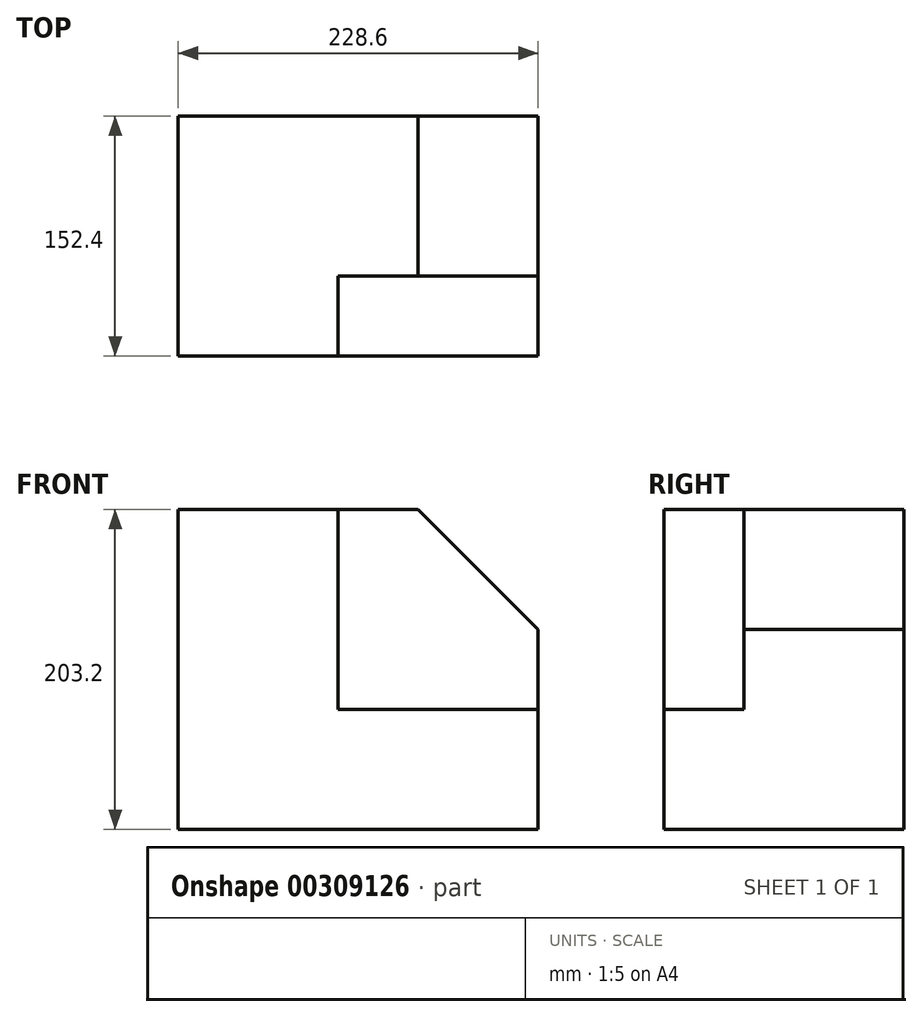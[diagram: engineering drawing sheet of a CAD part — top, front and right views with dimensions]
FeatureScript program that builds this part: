
annotation { "Feature Type Name" : "Feature", "Feature Type Description" : "" }
export const myFeature = defineFeature(function(context is Context, id is Id, definition is map)
    precondition{}
    {
        {
            var Q0;
            Q0=qCreatedBy(makeId("Top.planeOp"),FACE);
            var sketch = newSketch(context, id + "F0", { "sketchPlane" : qUnion([Q0])});
            skLineSegment(sketch, "E0.bottom", {"start": v(-104.27, 61.17) * mm, "end": v(124.33, 61.17) * mm});
            skLineSegment(sketch, "E0.top", {"start": v(-104.27, -91.23) * mm, "end": v(124.33, -91.23) * mm});
            skLineSegment(sketch, "E0.left", {"start": v(-104.27, 61.17) * mm, "end": v(-104.27, -91.23) * mm});
            skLineSegment(sketch, "E0.right", {"start": v(124.33, 61.17) * mm, "end": v(124.33, -91.23) * mm});
            skSolve(sketch);
        }
        {
            var Q0;
            Q0 = qSketchRegion(id + "F0", true);
            extrude(context, id + "F1", {"entities" : qUnion([Q0]), "depth" : 203.2 * mm});
        }
        {
            var Q0;
            Q0=makeQuery(id+"F1.opExtrude","CAP_FACE",FACE,{"disambiguationData":[OSD([sQuery(id+"F0.wireOp",EDGE,"E0.bottom"),sQuery(id+"F0.wireOp",EDGE,"E0.top"),sQuery(id+"F0.wireOp",EDGE,"E0.left"),sQuery(id+"F0.wireOp",EDGE,"E0.right")])],"isStart":false});
            var sketch = newSketch(context, id + "F2", { "sketchPlane" : qUnion([Q0])});
            skLineSegment(sketch, "E1.bottom", {"start": v(-2.67, -40.43) * mm, "end": v(124.33, -40.43) * mm});
            skLineSegment(sketch, "E1.top", {"start": v(-2.67, -91.23) * mm, "end": v(124.33, -91.23) * mm});
            skLineSegment(sketch, "E1.left", {"start": v(-2.67, -40.43) * mm, "end": v(-2.67, -91.23) * mm});
            skLineSegment(sketch, "E1.right", {"start": v(124.33, -40.43) * mm, "end": v(124.33, -91.23) * mm});
            skSolve(sketch);
        }
        {
            var Q0;
            Q0=makeQuery(id+"F2.imprint","IMPRINT",FACE,{"disambiguationData":[TD([[makeQuery(id+"F2.imprint","IMPRINT",EDGE,{"derivedFrom":sQuery(id+"F2.wireOp",EDGE,"E1.bottom")}),-1.0]])]});
            var Q1;
            Q1 = qSketchRegion(id + "F4", true);
            extrude(context, id + "F3", {"entities" : qUnion([Q0, Q1]), "operationType" : NewBodyOperationType.REMOVE, "oppositeDirection" : true, "depth" : 127 * mm});
        }
        {
            var Q0;
            Q0=makeQuery(id+"F3.boolean.opBoolean","COPY",FACE,{"derivedFrom":makeQuery(id+"F3.opExtrude","SWEPT_FACE",FACE,{"disambiguationData":[OSD([sQuery(id+"F2.wireOp",EDGE,"E1.bottom")])]})});
            var sketch = newSketch(context, id + "F4", { "sketchPlane" : qUnion([Q0])});
            skLineSegment(sketch, "E2", {"start": v(48.13, 203.2) * mm, "end": v(124.33, 127) * mm});
            skLineSegment(sketch, "E3", {"start": v(48.13, 203.2) * mm, "end": v(48.13, 76.2) * mm});
            skLineSegment(sketch, "E4", {"start": v(124.33, 127) * mm, "end": v(48.13, 127) * mm});
            skLineSegment(sketch, "E5", {"start": v(124.33, 127) * mm, "end": v(124.33, 76.2) * mm});
            skLineSegment(sketch, "E6", {"start": v(124.33, 76.2) * mm, "end": v(124.33, 0) * mm});
            skSolve(sketch);
        }
        {
            var Q0;
            {var subQ0=sQuery(id+"F4.wireOp",EDGE,"E2");Q0=makeQuery(id+"F4.imprint","IMPRINT",FACE,{"disambiguationData":[TD([[makeQuery(id+"F4.imprint","IMPRINT",EDGE,{"derivedFrom":subQ0}),1.0]])]});}
            extrude(context, id + "F5", {"entities" : qUnion([Q0]), "operationType" : NewBodyOperationType.REMOVE, "oppositeDirection" : true, "depth" : 101.6 * mm});
        }
    });
